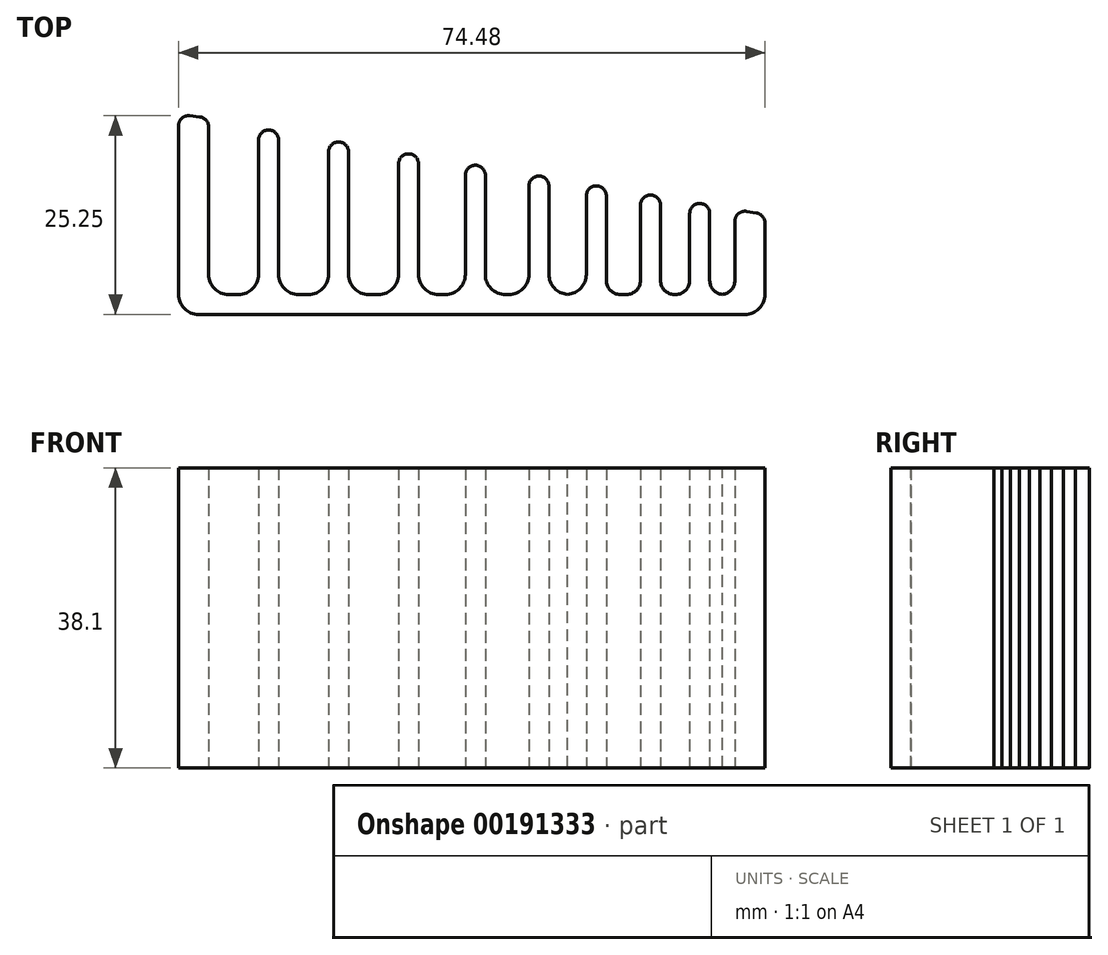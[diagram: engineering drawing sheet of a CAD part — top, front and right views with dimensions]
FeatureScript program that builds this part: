
annotation { "Feature Type Name" : "Feature", "Feature Type Description" : "" }
export const myFeature = defineFeature(function(context is Context, id is Id, definition is map)
    precondition{}
    {
        {
            var Q0;
            Q0=qCreatedBy(makeId("Top.planeOp"),FACE);
            var sketch = newSketch(context, id + "F0", { "sketchPlane" : qUnion([Q0])});
            skLineSegment(sketch, "E0", {"start": v(-37.24, 0) * mm, "end": v(37.24, 0) * mm});
            skPoint(sketch, "E1", {"position": v(0, 0) * mm});
            skLineSegment(sketch, "E2", {"start": v(-37.24, 0) * mm, "end": v(-37.24, 25.4) * mm});
            skLineSegment(sketch, "E3", {"start": v(37.24, 0) * mm, "end": v(37.24, 12.7) * mm});
            skPoint(sketch, "E4", {"position": v(-33.43, 24.98) * mm});
            skLineSegment(sketch, "E5", {"start": v(-37.24, 25.4) * mm, "end": v(-33.43, 24.98) * mm});
            skLineSegment(sketch, "E6", {"start": v(-33.43, 24.98) * mm, "end": v(-33.43, 2.54) * mm});
            skLineSegment(sketch, "E7", {"start": v(-37.24, 25.4) * mm, "end": v(37.24, 12.7) * mm, "construction": true});
            skLineSegment(sketch, "E8", {"start": v(-37.24, 2.54) * mm, "end": v(37.24, 2.54) * mm, "construction": true});
            skLineSegment(sketch, "E9", {"start": v(-27.08, 2.54) * mm, "end": v(-27.08, 23.67) * mm});
            skLineSegment(sketch, "E10", {"start": v(-27.08, 23.67) * mm, "end": v(-24.54, 23.23) * mm});
            skLineSegment(sketch, "E11", {"start": v(-24.54, 23.23) * mm, "end": v(-24.54, 2.54) * mm});
            skLineSegment(sketch, "E12", {"start": v(-24.54, 2.54) * mm, "end": v(-18.19, 2.54) * mm});
            skLineSegment(sketch, "E13", {"start": v(-18.19, 2.54) * mm, "end": v(-18.19, 22.15) * mm});
            skLineSegment(sketch, "E14", {"start": v(-18.19, 22.15) * mm, "end": v(-15.65, 21.72) * mm});
            skLineSegment(sketch, "E15", {"start": v(-15.65, 21.72) * mm, "end": v(-15.65, 2.54) * mm});
            skLineSegment(sketch, "E16", {"start": v(-15.65, 2.54) * mm, "end": v(-9.3, 2.54) * mm});
            skLineSegment(sketch, "E17", {"start": v(-9.3, 2.54) * mm, "end": v(-9.3, 20.64) * mm});
            skLineSegment(sketch, "E18", {"start": v(-9.3, 20.64) * mm, "end": v(-6.76, 20.2) * mm});
            skLineSegment(sketch, "E19", {"start": v(-6.76, 20.2) * mm, "end": v(-6.76, 2.54) * mm});
            skLineSegment(sketch, "E20", {"start": v(-6.76, 2.54) * mm, "end": v(-0.81, 2.54) * mm});
            skLineSegment(sketch, "E21", {"start": v(-0.81, 2.54) * mm, "end": v(-0.81, 19.19) * mm});
            skLineSegment(sketch, "E22", {"start": v(-0.81, 19.19) * mm, "end": v(1.73, 18.76) * mm});
            skLineSegment(sketch, "E23", {"start": v(1.73, 18.76) * mm, "end": v(1.73, 2.54) * mm});
            skLineSegment(sketch, "E24", {"start": v(1.73, 2.54) * mm, "end": v(7.26, 2.54) * mm});
            skLineSegment(sketch, "E25", {"start": v(7.26, 2.54) * mm, "end": v(7.26, 17.81) * mm});
            skLineSegment(sketch, "E26", {"start": v(7.26, 17.81) * mm, "end": v(9.8, 17.38) * mm});
            skLineSegment(sketch, "E27", {"start": v(9.8, 17.38) * mm, "end": v(9.8, 2.54) * mm});
            skLineSegment(sketch, "E28", {"start": v(9.8, 2.54) * mm, "end": v(14.55, 2.54) * mm});
            skLineSegment(sketch, "E29", {"start": v(14.55, 2.54) * mm, "end": v(14.55, 16.57) * mm});
            skLineSegment(sketch, "E30", {"start": v(14.55, 16.57) * mm, "end": v(17.1, 16.13) * mm});
            skLineSegment(sketch, "E31", {"start": v(17.1, 16.13) * mm, "end": v(17.1, 2.54) * mm});
            skLineSegment(sketch, "E32", {"start": v(17.1, 2.54) * mm, "end": v(21.44, 2.54) * mm});
            skLineSegment(sketch, "E33", {"start": v(21.44, 2.54) * mm, "end": v(21.44, 15.4) * mm});
            skLineSegment(sketch, "E34", {"start": v(21.44, 15.4) * mm, "end": v(23.98, 14.96) * mm});
            skLineSegment(sketch, "E35", {"start": v(23.98, 14.96) * mm, "end": v(23.98, 2.54) * mm});
            skLineSegment(sketch, "E36", {"start": v(23.98, 2.54) * mm, "end": v(27.69, 2.54) * mm});
            skLineSegment(sketch, "E37", {"start": v(27.69, 2.54) * mm, "end": v(27.69, 14.33) * mm});
            skLineSegment(sketch, "E38", {"start": v(27.69, 14.33) * mm, "end": v(30.23, 13.9) * mm});
            skLineSegment(sketch, "E39", {"start": v(30.23, 13.9) * mm, "end": v(30.23, 2.54) * mm});
            skLineSegment(sketch, "E40", {"start": v(30.23, 2.54) * mm, "end": v(33.43, 2.54) * mm});
            skLineSegment(sketch, "E41", {"start": v(33.43, 2.54) * mm, "end": v(33.43, 13.35) * mm});
            skLineSegment(sketch, "E42", {"start": v(33.43, 13.35) * mm, "end": v(37.24, 12.7) * mm});
            skLineSegment(sketch, "E43", {"start": v(-27.08, 2.54) * mm, "end": v(-33.43, 2.54) * mm});
            skSolve(sketch);
        }
        {
            var Q0;
            Q0 = qSketchRegion(id + "F0", true);
            extrude(context, id + "F1", {"entities" : qUnion([Q0]), "depth" : 38.1 * mm});
        }
        {
            var Q0;
            Q0=makeQuery(id+"F1.opExtrude","SWEPT_EDGE",EDGE,{"disambiguationData":[OSD([sQuery(id+"F0.wireOp",EDGE,"E6"),sQuery(id+"F0.wireOp",EDGE,"E43")])]});
            var Q1;
            Q1=makeQuery(id+"F1.opExtrude","SWEPT_EDGE",EDGE,{"disambiguationData":[OSD([sQuery(id+"F0.wireOp",EDGE,"E9"),sQuery(id+"F0.wireOp",EDGE,"E43")])]});
            var Q2;
            Q2=makeQuery(id+"F1.opExtrude","SWEPT_EDGE",EDGE,{"disambiguationData":[OSD([sQuery(id+"F0.wireOp",EDGE,"E11"),sQuery(id+"F0.wireOp",EDGE,"E12")])]});
            var Q3;
            Q3=makeQuery(id+"F1.opExtrude","SWEPT_EDGE",EDGE,{"disambiguationData":[OSD([sQuery(id+"F0.wireOp",EDGE,"E12"),sQuery(id+"F0.wireOp",EDGE,"E13")])]});
            var Q4;
            Q4=makeQuery(id+"F1.opExtrude","SWEPT_EDGE",EDGE,{"disambiguationData":[OSD([sQuery(id+"F0.wireOp",EDGE,"E15"),sQuery(id+"F0.wireOp",EDGE,"E16")])]});
            var Q5;
            Q5=makeQuery(id+"F1.opExtrude","SWEPT_EDGE",EDGE,{"disambiguationData":[OSD([sQuery(id+"F0.wireOp",EDGE,"E16"),sQuery(id+"F0.wireOp",EDGE,"E17")])]});
            var Q6;
            Q6=makeQuery(id+"F1.opExtrude","SWEPT_EDGE",EDGE,{"disambiguationData":[OSD([sQuery(id+"F0.wireOp",EDGE,"E19"),sQuery(id+"F0.wireOp",EDGE,"E20")])]});
            var Q7;
            Q7=makeQuery(id+"F1.opExtrude","SWEPT_EDGE",EDGE,{"disambiguationData":[OSD([sQuery(id+"F0.wireOp",EDGE,"E20"),sQuery(id+"F0.wireOp",EDGE,"E21")])]});
            var Q8;
            Q8=makeQuery(id+"F1.opExtrude","SWEPT_EDGE",EDGE,{"disambiguationData":[OSD([sQuery(id+"F0.wireOp",EDGE,"E23"),sQuery(id+"F0.wireOp",EDGE,"E24")])]});
            var Q9;
            Q9=makeQuery(id+"F1.opExtrude","SWEPT_EDGE",EDGE,{"disambiguationData":[OSD([sQuery(id+"F0.wireOp",EDGE,"E24"),sQuery(id+"F0.wireOp",EDGE,"E25")])]});
            var Q10;
            Q10=makeQuery(id+"F1.opExtrude","SWEPT_EDGE",EDGE,{"disambiguationData":[OSD([sQuery(id+"F0.wireOp",EDGE,"E27"),sQuery(id+"F0.wireOp",EDGE,"E28")])]});
            var Q11;
            Q11=makeQuery(id+"F1.opExtrude","SWEPT_EDGE",EDGE,{"disambiguationData":[OSD([sQuery(id+"F0.wireOp",EDGE,"E28"),sQuery(id+"F0.wireOp",EDGE,"E29")])]});
            var Q12;
            Q12=makeQuery(id+"F1.opExtrude","SWEPT_EDGE",EDGE,{"disambiguationData":[OSD([sQuery(id+"F0.wireOp",EDGE,"E0"),sQuery(id+"F0.wireOp",EDGE,"E2")])]});
            var Q13;
            Q13=makeQuery(id+"F1.opExtrude","SWEPT_EDGE",EDGE,{"disambiguationData":[OSD([sQuery(id+"F0.wireOp",EDGE,"E0"),sQuery(id+"F0.wireOp",EDGE,"E3")])]});
            fillet(context, id + "F2", {"entities" : qUnion([Q0, Q1, Q2, Q3, Q4, Q5, Q6, Q7, Q8, Q9, Q10, Q11, Q12, Q13]), "radius" : 2.54 * mm, "tangentPropagation" : true, "allowEdgeOverflow" : false});
        }
        {
            var Q0;
            Q0=makeQuery(id+"F1.opExtrude","SWEPT_EDGE",EDGE,{"disambiguationData":[OSD([sQuery(id+"F0.wireOp",EDGE,"E31"),sQuery(id+"F0.wireOp",EDGE,"E32")])]});
            var Q1;
            Q1=makeQuery(id+"F1.opExtrude","SWEPT_EDGE",EDGE,{"disambiguationData":[OSD([sQuery(id+"F0.wireOp",EDGE,"E32"),sQuery(id+"F0.wireOp",EDGE,"E33")])]});
            var Q2;
            Q2=makeQuery(id+"F1.opExtrude","SWEPT_EDGE",EDGE,{"disambiguationData":[OSD([sQuery(id+"F0.wireOp",EDGE,"E35"),sQuery(id+"F0.wireOp",EDGE,"E36")])]});
            var Q3;
            Q3=makeQuery(id+"F1.opExtrude","SWEPT_EDGE",EDGE,{"disambiguationData":[OSD([sQuery(id+"F0.wireOp",EDGE,"E36"),sQuery(id+"F0.wireOp",EDGE,"E37")])]});
            var Q4;
            Q4=makeQuery(id+"F1.opExtrude","SWEPT_EDGE",EDGE,{"disambiguationData":[OSD([sQuery(id+"F0.wireOp",EDGE,"E39"),sQuery(id+"F0.wireOp",EDGE,"E40")])]});
            var Q5;
            Q5=makeQuery(id+"F1.opExtrude","SWEPT_EDGE",EDGE,{"disambiguationData":[OSD([sQuery(id+"F0.wireOp",EDGE,"E40"),sQuery(id+"F0.wireOp",EDGE,"E41")])]});
            fillet(context, id + "F3", {"entities" : qUnion([Q0, Q1, Q2, Q3, Q4, Q5]), "radius" : 1.78 * mm, "tangentPropagation" : true, "allowEdgeOverflow" : false});
        }
        {
            var Q0;
            Q0=makeQuery(id+"F1.opExtrude","SWEPT_EDGE",EDGE,{"disambiguationData":[OSD([sQuery(id+"F0.wireOp",EDGE,"E41"),sQuery(id+"F0.wireOp",EDGE,"E42")])]});
            var Q1;
            Q1=makeQuery(id+"F1.opExtrude","SWEPT_EDGE",EDGE,{"disambiguationData":[OSD([sQuery(id+"F0.wireOp",EDGE,"E38"),sQuery(id+"F0.wireOp",EDGE,"E39")])]});
            var Q2;
            Q2=makeQuery(id+"F1.opExtrude","SWEPT_EDGE",EDGE,{"disambiguationData":[OSD([sQuery(id+"F0.wireOp",EDGE,"E37"),sQuery(id+"F0.wireOp",EDGE,"E38")])]});
            var Q3;
            Q3=makeQuery(id+"F1.opExtrude","SWEPT_EDGE",EDGE,{"disambiguationData":[OSD([sQuery(id+"F0.wireOp",EDGE,"E34"),sQuery(id+"F0.wireOp",EDGE,"E35")])]});
            var Q4;
            Q4=makeQuery(id+"F1.opExtrude","SWEPT_EDGE",EDGE,{"disambiguationData":[OSD([sQuery(id+"F0.wireOp",EDGE,"E33"),sQuery(id+"F0.wireOp",EDGE,"E34")])]});
            var Q5;
            Q5=makeQuery(id+"F1.opExtrude","SWEPT_EDGE",EDGE,{"disambiguationData":[OSD([sQuery(id+"F0.wireOp",EDGE,"E30"),sQuery(id+"F0.wireOp",EDGE,"E31")])]});
            var Q6;
            Q6=makeQuery(id+"F1.opExtrude","SWEPT_EDGE",EDGE,{"disambiguationData":[OSD([sQuery(id+"F0.wireOp",EDGE,"E29"),sQuery(id+"F0.wireOp",EDGE,"E30")])]});
            var Q7;
            Q7=makeQuery(id+"F1.opExtrude","SWEPT_EDGE",EDGE,{"disambiguationData":[OSD([sQuery(id+"F0.wireOp",EDGE,"E26"),sQuery(id+"F0.wireOp",EDGE,"E27")])]});
            var Q8;
            Q8=makeQuery(id+"F1.opExtrude","SWEPT_EDGE",EDGE,{"disambiguationData":[OSD([sQuery(id+"F0.wireOp",EDGE,"E25"),sQuery(id+"F0.wireOp",EDGE,"E26")])]});
            var Q9;
            Q9=makeQuery(id+"F1.opExtrude","SWEPT_EDGE",EDGE,{"disambiguationData":[OSD([sQuery(id+"F0.wireOp",EDGE,"E22"),sQuery(id+"F0.wireOp",EDGE,"E23")])]});
            var Q10;
            Q10=makeQuery(id+"F1.opExtrude","SWEPT_EDGE",EDGE,{"disambiguationData":[OSD([sQuery(id+"F0.wireOp",EDGE,"E21"),sQuery(id+"F0.wireOp",EDGE,"E22")])]});
            var Q11;
            Q11=makeQuery(id+"F1.opExtrude","SWEPT_EDGE",EDGE,{"disambiguationData":[OSD([sQuery(id+"F0.wireOp",EDGE,"E18"),sQuery(id+"F0.wireOp",EDGE,"E19")])]});
            var Q12;
            Q12=makeQuery(id+"F1.opExtrude","SWEPT_EDGE",EDGE,{"disambiguationData":[OSD([sQuery(id+"F0.wireOp",EDGE,"E14"),sQuery(id+"F0.wireOp",EDGE,"E15")])]});
            var Q13;
            Q13=makeQuery(id+"F1.opExtrude","SWEPT_EDGE",EDGE,{"disambiguationData":[OSD([sQuery(id+"F0.wireOp",EDGE,"E10"),sQuery(id+"F0.wireOp",EDGE,"E11")])]});
            var Q14;
            Q14=makeQuery(id+"F1.opExtrude","SWEPT_EDGE",EDGE,{"disambiguationData":[OSD([sQuery(id+"F0.wireOp",EDGE,"E9"),sQuery(id+"F0.wireOp",EDGE,"E10")])]});
            var Q15;
            Q15=makeQuery(id+"F1.opExtrude","SWEPT_EDGE",EDGE,{"disambiguationData":[OSD([sQuery(id+"F0.wireOp",EDGE,"E5"),sQuery(id+"F0.wireOp",EDGE,"E6")])]});
            var Q16;
            Q16=makeQuery(id+"F1.opExtrude","SWEPT_EDGE",EDGE,{"disambiguationData":[OSD([sQuery(id+"F0.wireOp",EDGE,"E2"),sQuery(id+"F0.wireOp",EDGE,"E5")])]});
            var Q17;
            Q17=makeQuery(id+"F1.opExtrude","SWEPT_EDGE",EDGE,{"disambiguationData":[OSD([sQuery(id+"F0.wireOp",EDGE,"E3"),sQuery(id+"F0.wireOp",EDGE,"E42")])]});
            var Q18;
            Q18=makeQuery(id+"F1.opExtrude","SWEPT_EDGE",EDGE,{"disambiguationData":[OSD([sQuery(id+"F0.wireOp",EDGE,"E17"),sQuery(id+"F0.wireOp",EDGE,"E18")])]});
            var Q19;
            Q19=makeQuery(id+"F1.opExtrude","SWEPT_EDGE",EDGE,{"disambiguationData":[OSD([sQuery(id+"F0.wireOp",EDGE,"E13"),sQuery(id+"F0.wireOp",EDGE,"E14")])]});
            fillet(context, id + "F4", {"entities" : qUnion([Q0, Q1, Q2, Q3, Q4, Q5, Q6, Q7, Q8, Q9, Q10, Q11, Q12, Q13, Q14, Q15, Q16, Q17, Q18, Q19]), "radius" : 1.27 * mm, "tangentPropagation" : true, "allowEdgeOverflow" : false});
        }
    });
